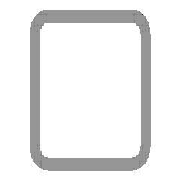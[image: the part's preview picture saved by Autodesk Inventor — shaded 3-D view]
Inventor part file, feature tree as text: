
AUTODESK INVENTOR PART (.ipt)
format: ipt  version: 2025.3 (Build 293356030, 356C)  size: 134,144 bytes
history: native  units: mm (DEFAULTED — no unit token found)
features: other x4, sketch x1, plane x1
ambient origin geometry x8: Origin, YZ Plane, XZ Plane, XY Plane, X Axis, Y Axis, Z Axis, Center Point
bodies: Solid1 (feature_tree), Body (feature_tree)
feature tree (6):
  parser-record x1  (decoder bookkeeping rows leaked as tree rows — omitted from the tree; the rows remain in map.json)
  other  "Driven Length"
  other  "Start Plane"
  other  "End Plane"
  sketch  "Sketch3"  dims[d3=2200.0mm d4=0.0mm d7=6.0mm d9=100.0mm d11=100.0mm d12=3.0mm d13=-0.0mm d14=2200.0mm d15=50.0mm d16=50.0mm d17=90.0deg d18=2200.0mm]
  plane  "Work Plane3"
